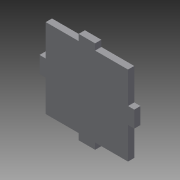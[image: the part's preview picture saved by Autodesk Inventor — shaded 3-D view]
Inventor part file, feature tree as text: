
AUTODESK INVENTOR PART (.ipt)
format: ipt  version: 2015 SP1 (Build 190203100, 203)  size: 98,816 bytes
history: native  units: in
note: dims shown in document units (in); Inventor stores cm internally (conversion verified against a paired STEP export)
features: reference x8, sketch x3, plane x2, extrude x1
ambient origin geometry x8: Origin, YZ Plane, XZ Plane, XY Plane, X Axis, Y Axis, Z Axis, Center Point
bodies: Body1 (feature_tree)
feature tree (14):
  sketch  "Sketch1"  dims[d2=0.19in d3=0.0in]
  plane  "Work Plane2"
  sketch  "Sketch2"
  plane  "Work Plane1"
  sketch  "Sketch3"
  extrude  "Extrusion2"  [1 undecoded]
  reference  "Reference1"
  reference  "Reference2"
  reference  "Reference3"
  reference  "Reference4"
  reference  "Reference5"
  reference  "Reference6"
  reference  "Reference9"
  reference  "Reference10"
note: 1 required parameter value undecoded (feature->parameter linkage not recoverable at this tier; creation-order binding heuristic only, values carry confidence <= 0.55)
